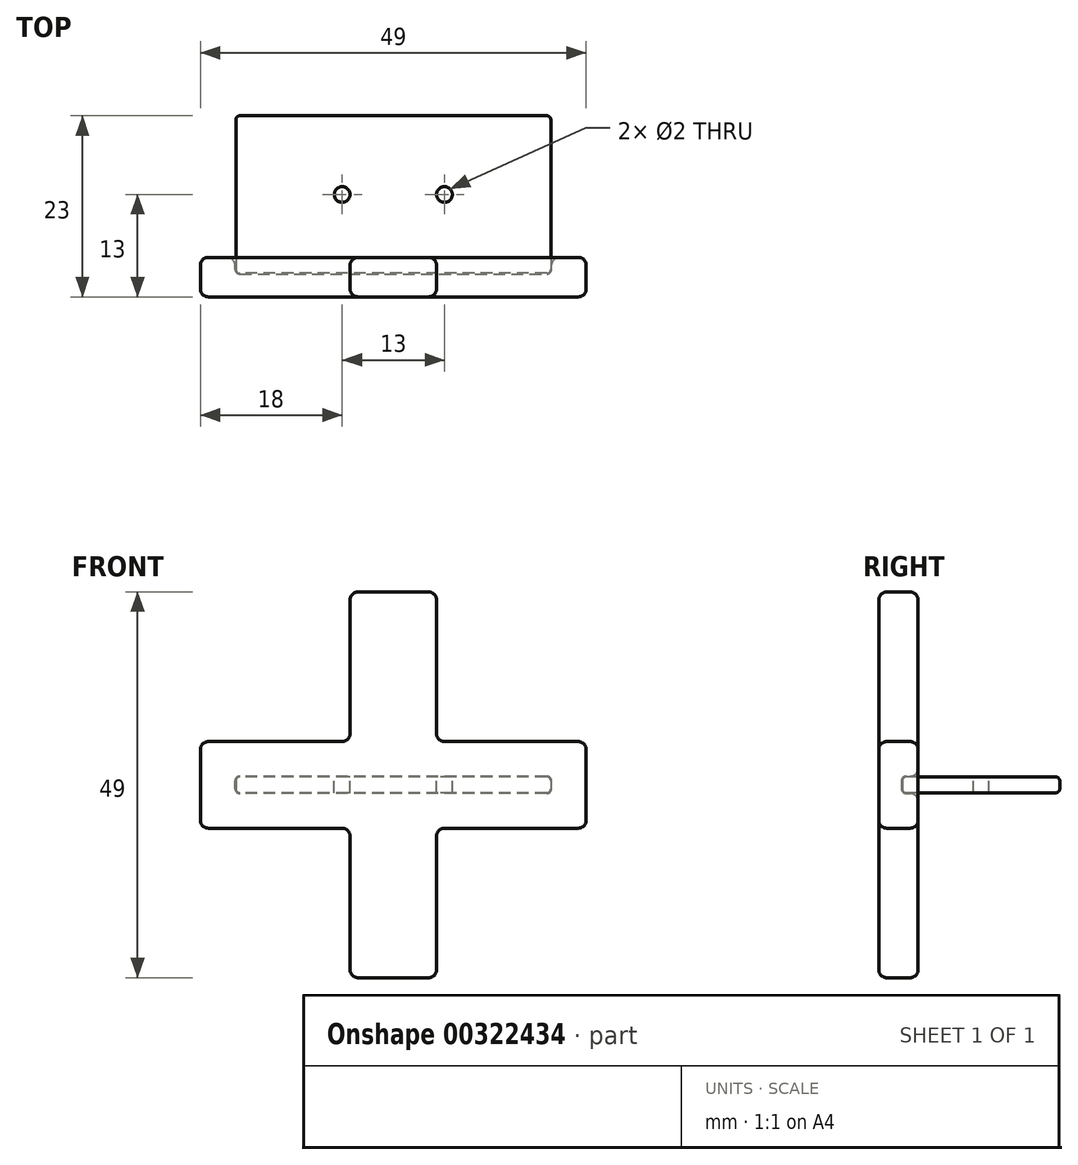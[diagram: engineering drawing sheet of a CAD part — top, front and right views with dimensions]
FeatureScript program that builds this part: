
annotation { "Feature Type Name" : "Feature", "Feature Type Description" : "" }
export const myFeature = defineFeature(function(context is Context, id is Id, definition is map)
    precondition{}
    {
        {
            var Q0;
            Q0=qCreatedBy(makeId("Top.planeOp"),FACE);
            var sketch = newSketch(context, id + "F0", { "sketchPlane" : qUnion([Q0])});
            skLineSegment(sketch, "E0.bottom", {"start": v(20, 10) * mm, "end": v(-20, 10) * mm});
            skLineSegment(sketch, "E0.top", {"start": v(20, -10) * mm, "end": v(-20, -10) * mm});
            skLineSegment(sketch, "E0.left", {"start": v(20, 10) * mm, "end": v(20, -10) * mm});
            skLineSegment(sketch, "E0.right", {"start": v(-20, 10) * mm, "end": v(-20, -10) * mm});
            skPoint(sketch, "E0.middle", {"position": v(0, 0) * mm});
            skSolve(sketch);
        }
        {
            var Q0;
            Q0=makeQuery(id+"F0.imprint","IMPRINT",FACE,{"disambiguationData":[TD([[makeQuery(id+"F0.imprint","IMPRINT",EDGE,{"derivedFrom":sQuery(id+"F0.wireOp",EDGE,"E0.bottom")}),1.0]])]});
            extrude(context, id + "F1", {"entities" : qUnion([Q0]), "depth" : 2 * mm});
        }
        {
            var Q0;
            Q0=makeQuery(id+"F1.opExtrude","SWEPT_FACE",FACE,{"disambiguationData":[OSD([sQuery(id+"F0.wireOp",EDGE,"E0.top")])]});
            var Q1;
            Q1=makeQuery(id+"F1.opExtrude","CAP_FACE",FACE,{"disambiguationData":[OSD([sQuery(id+"F0.wireOp",EDGE,"E0.bottom"),sQuery(id+"F0.wireOp",EDGE,"E0.top"),sQuery(id+"F0.wireOp",EDGE,"E0.left"),sQuery(id+"F0.wireOp",EDGE,"E0.right")])],"isStart":false});
            var Q2;
            Q2=makeQuery(id+"F1.opExtrude","CAP_FACE",FACE,{"disambiguationData":[OSD([sQuery(id+"F0.wireOp",EDGE,"E0.bottom"),sQuery(id+"F0.wireOp",EDGE,"E0.top"),sQuery(id+"F0.wireOp",EDGE,"E0.left"),sQuery(id+"F0.wireOp",EDGE,"E0.right")])],"isStart":true});
            var Q3;
            Q3=makeQuery(id+"F1.opExtrude","SWEPT_FACE",FACE,{"disambiguationData":[OSD([sQuery(id+"F0.wireOp",EDGE,"E0.right")])]});
            var Q4;
            Q4=makeQuery(id+"F1.opExtrude","SWEPT_FACE",FACE,{"disambiguationData":[OSD([sQuery(id+"F0.wireOp",EDGE,"E0.bottom")])]});
            var Q5;
            Q5=makeQuery(id+"F1.opExtrude","SWEPT_FACE",FACE,{"disambiguationData":[OSD([sQuery(id+"F0.wireOp",EDGE,"E0.left")])]});
            fillet(context, id + "F2", {"entities" : qUnion([Q0, Q1, Q2, Q3, Q4, Q5]), "radius" : 0.5 * mm, "tangentPropagation" : true, "allowEdgeOverflow" : false});
        }
        {
            var Q0;
            Q0=makeQuery(id+"F1.opExtrude","CAP_FACE",FACE,{"disambiguationData":[OSD([sQuery(id+"F0.wireOp",EDGE,"E0.bottom"),sQuery(id+"F0.wireOp",EDGE,"E0.top"),sQuery(id+"F0.wireOp",EDGE,"E0.left"),sQuery(id+"F0.wireOp",EDGE,"E0.right")])],"isStart":false});
            var sketch = newSketch(context, id + "F3", { "sketchPlane" : qUnion([Q0])});
            skCircle(sketch, "E1", {"center": v(-6.5, 0) * mm, "radius": 1 * mm});
            skCircle(sketch, "E2", {"center": v(6.5, 0) * mm, "radius": 1 * mm});
            skSolve(sketch);
        }
        {
            var Q0;
            Q0=makeQuery(id+"F3.imprint","IMPRINT",FACE,{"disambiguationData":[TD([[makeQuery(id+"F3.imprint","IMPRINT",EDGE,{"derivedFrom":sQuery(id+"F3.wireOp",EDGE,"E1")}),1.0]])]});
            var Q1;
            Q1=makeQuery(id+"F3.imprint","IMPRINT",FACE,{"disambiguationData":[TD([[makeQuery(id+"F3.imprint","IMPRINT",EDGE,{"derivedFrom":sQuery(id+"F3.wireOp",EDGE,"E2")}),1.0]])]});
            extrude(context, id + "F4", {"entities" : qUnion([Q0, Q1]), "operationType" : NewBodyOperationType.REMOVE, "oppositeDirection" : true, "depth" : 25 * mm});
        }
        {
            var Q0;
            Q0=makeQuery(id+"F1.opExtrude","SWEPT_FACE",FACE,{"disambiguationData":[OSD([sQuery(id+"F0.wireOp",EDGE,"E0.top")])]});
            var sketch = newSketch(context, id + "F5", { "sketchPlane" : qUnion([Q0])});
            skSolve(sketch);
        }
        {
            var Q0;
            {var subQ0=sQuery(id+"F0.wireOp",EDGE,"E0.top");var subQ1=makeQuery(id+"F1.opExtrude","SWEPT_FACE",FACE,{"disambiguationData":[OSD([subQ0])]});Q0=makeQuery(id+"F5.imprint","IMPRINT",FACE,{"disambiguationData":[TD([[makeQuery(id+"F5.imprint","IMPRINT",EDGE,{"derivedFrom":makeQuery(id+"F2.opFillet","BLEND_EDGE",EDGE,{"blendedFrom":[makeQuery(id+"F1.opExtrude","CAP_EDGE",EDGE,{"disambiguationData":[OSD([subQ0])],"isStart":true}),subQ1],"blendedInto":[subQ1]})}),1.0]])]});}
            var sketch = newSketch(context, id + "F6", { "sketchPlane" : qUnion([Q0])});
            skLineSegment(sketch, "E3.0", {"start": v(24.5, 6.5) * mm, "end": v(5.5, 6.5) * mm});
            skLineSegment(sketch, "E3.1", {"start": v(24.5, -4.5) * mm, "end": v(24.5, 6.5) * mm});
            skLineSegment(sketch, "E3.2", {"start": v(-24.5, -4.5) * mm, "end": v(24.5, -4.5) * mm});
            skLineSegment(sketch, "E3.3", {"start": v(-24.5, 6.5) * mm, "end": v(-24.5, -4.5) * mm});
            skLineSegment(sketch, "E4.bottom", {"start": v(5.5, -23.5) * mm, "end": v(-5.5, -23.5) * mm});
            skLineSegment(sketch, "E4.top", {"start": v(5.5, 25.5) * mm, "end": v(-5.5, 25.5) * mm});
            skLineSegment(sketch, "E4.left", {"start": v(5.5, -23.5) * mm, "end": v(5.5, -4.5) * mm});
            skLineSegment(sketch, "E4.right", {"start": v(-5.5, -23.5) * mm, "end": v(-5.5, -4.5) * mm});
            skPoint(sketch, "E4.middle", {"position": v(0, 6.5) * mm});
            skLineSegment(sketch, "E5.trimOffspring", {"start": v(-5.5, 6.5) * mm, "end": v(-24.5, 6.5) * mm});
            skLineSegment(sketch, "E6.trimOffspring", {"start": v(5.5, 6.5) * mm, "end": v(5.5, 25.5) * mm});
            skLineSegment(sketch, "E7.trimOffspring", {"start": v(-5.5, 6.5) * mm, "end": v(-5.5, 25.5) * mm});
            skPoint(sketch, "E8.0.3.end.orphan", {"position": v(19.5, 1.5) * mm});
            skPoint(sketch, "E8.0.3.start.orphan", {"position": v(19.5, 0.5) * mm});
            skPoint(sketch, "E8.0.1.end.orphan", {"position": v(-19.5, 0.5) * mm});
            skPoint(sketch, "E8.0.1.start.orphan", {"position": v(-19.5, 1.5) * mm});
            skSolve(sketch);
        }
        {
            var Q0;
            {var subQ0=sQuery(id+"F0.wireOp",EDGE,"E0.top");var subQ1=makeQuery(id+"F1.opExtrude","SWEPT_FACE",FACE,{"disambiguationData":[OSD([subQ0])]});Q0=makeQuery(id+"F6.imprint","IMPRINT",FACE,{"disambiguationData":[TD([[makeQuery(id+"F6.imprint","IMPRINT",EDGE,{"derivedFrom":makeQuery(id+"F5.imprint","IMPRINT",EDGE,{"derivedFrom":makeQuery(id+"F2.opFillet","BLEND_EDGE",EDGE,{"blendedFrom":[makeQuery(id+"F1.opExtrude","CAP_EDGE",EDGE,{"disambiguationData":[OSD([subQ0])],"isStart":true}),subQ1],"blendedInto":[subQ1]})})}),1.0]])]});}
            var Q1;
            Q1=makeQuery(id+"F6.imprint","IMPRINT",FACE,{"disambiguationData":[TD([[makeQuery(id+"F6.imprint","IMPRINT",EDGE,{"derivedFrom":sQuery(id+"F6.wireOp",EDGE,"E3.0")}),1.0]])]});
            var Q2;
            Q2=makeQuery(id+"F6.imprint","IMPRINT",FACE,{"disambiguationData":[TD([[makeQuery(id+"F6.imprint","IMPRINT",EDGE,{"derivedFrom":sQuery(id+"F6.wireOp",EDGE,"E4.bottom")}),-1.0]])]});
            extrude(context, id + "F7", {"entities" : qUnion([Q0, Q1, Q2]), "depth" : 3 * mm, "hasSecondDirection" : true, "secondDirectionOppositeDirection" : true, "secondDirectionDepth" : 2 * mm});
        }
        {
            var Q0;
            Q0=makeQuery(id+"F1.opExtrude","SWEPT_BODY",BODY,{"disambiguationData":[OSD([sQuery(id+"F0.wireOp",EDGE,"E0.bottom"),sQuery(id+"F0.wireOp",EDGE,"E0.top"),sQuery(id+"F0.wireOp",EDGE,"E0.left"),sQuery(id+"F0.wireOp",EDGE,"E0.right")])]});
            var Q1;
            Q1=makeQuery(id+"F7.opExtrude","SWEPT_BODY",BODY,{"disambiguationData":[OSD([sQuery(id+"F6.wireOp",EDGE,"E3.0"),sQuery(id+"F6.wireOp",EDGE,"E3.1"),sQuery(id+"F6.wireOp",EDGE,"E3.2"),sQuery(id+"F6.wireOp",EDGE,"E3.3"),sQuery(id+"F6.wireOp",EDGE,"E4.bottom"),sQuery(id+"F6.wireOp",EDGE,"E4.top"),sQuery(id+"F6.wireOp",EDGE,"E4.left"),sQuery(id+"F6.wireOp",EDGE,"E4.right"),sQuery(id+"F6.wireOp",EDGE,"E5.trimOffspring"),sQuery(id+"F6.wireOp",EDGE,"E6.trimOffspring"),sQuery(id+"F6.wireOp",EDGE,"E7.trimOffspring")])]});
            booleanBodies(context, id + "F8", {"operationType" : BooleanOperationType.SUBTRACTION, "tools" : qUnion([Q0]), "targets" : qUnion([Q1]), "offset" : true, "offsetAll" : true, "offsetDistance" : 0.1 * mm, "keepTools" : true});
        }
        {
            var Q0;
            Q0=makeQuery(id+"F7.opExtrude","CAP_FACE",FACE,{"disambiguationData":[OSD([sQuery(id+"F6.wireOp",EDGE,"E3.0"),sQuery(id+"F6.wireOp",EDGE,"E3.1"),sQuery(id+"F6.wireOp",EDGE,"E3.2"),sQuery(id+"F6.wireOp",EDGE,"E3.3"),sQuery(id+"F6.wireOp",EDGE,"E4.bottom"),sQuery(id+"F6.wireOp",EDGE,"E4.top"),sQuery(id+"F6.wireOp",EDGE,"E4.left"),sQuery(id+"F6.wireOp",EDGE,"E4.right"),sQuery(id+"F6.wireOp",EDGE,"E5.trimOffspring"),sQuery(id+"F6.wireOp",EDGE,"E6.trimOffspring"),sQuery(id+"F6.wireOp",EDGE,"E7.trimOffspring")])],"isStart":true});
            var Q1;
            Q1=makeQuery(id+"F7.opExtrude","CAP_FACE",FACE,{"disambiguationData":[OSD([sQuery(id+"F6.wireOp",EDGE,"E3.0"),sQuery(id+"F6.wireOp",EDGE,"E3.1"),sQuery(id+"F6.wireOp",EDGE,"E3.2"),sQuery(id+"F6.wireOp",EDGE,"E3.3"),sQuery(id+"F6.wireOp",EDGE,"E4.bottom"),sQuery(id+"F6.wireOp",EDGE,"E4.top"),sQuery(id+"F6.wireOp",EDGE,"E4.left"),sQuery(id+"F6.wireOp",EDGE,"E4.right"),sQuery(id+"F6.wireOp",EDGE,"E5.trimOffspring"),sQuery(id+"F6.wireOp",EDGE,"E6.trimOffspring"),sQuery(id+"F6.wireOp",EDGE,"E7.trimOffspring")])],"isStart":false});
            var Q2;
            {var subQ0=sQuery(id+"F6.wireOp",EDGE,"E3.2");Q2=makeQuery(id+"F7.opExtrude","SWEPT_FACE",FACE,{"disambiguationData":[OSD([subQ0]),TDD([makeQuery(id+"F6.imprint","IMPRINT",EDGE,{"disambiguationData":[TD([[makeQuery(id+"F6.imprint","INTERSECT",VERTEX,{"derivedFrom":[sQuery(id+"F6.wireOp",EDGE,"E3.1"),subQ0]}),1.0]])],"derivedFrom":subQ0})])]});}
            var Q3;
            Q3=makeQuery(id+"F7.opExtrude","SWEPT_FACE",FACE,{"disambiguationData":[OSD([sQuery(id+"F6.wireOp",EDGE,"E4.left")])]});
            var Q4;
            Q4=makeQuery(id+"F7.opExtrude","SWEPT_FACE",FACE,{"disambiguationData":[OSD([sQuery(id+"F6.wireOp",EDGE,"E4.bottom")])]});
            var Q5;
            Q5=makeQuery(id+"F7.opExtrude","SWEPT_FACE",FACE,{"disambiguationData":[OSD([sQuery(id+"F6.wireOp",EDGE,"E3.1")])]});
            var Q6;
            Q6=makeQuery(id+"F7.opExtrude","SWEPT_FACE",FACE,{"disambiguationData":[OSD([sQuery(id+"F6.wireOp",EDGE,"E3.0")])]});
            var Q7;
            Q7=makeQuery(id+"F7.opExtrude","SWEPT_FACE",FACE,{"disambiguationData":[OSD([sQuery(id+"F6.wireOp",EDGE,"E6.trimOffspring")])]});
            var Q8;
            Q8=makeQuery(id+"F7.opExtrude","SWEPT_FACE",FACE,{"disambiguationData":[OSD([sQuery(id+"F6.wireOp",EDGE,"E4.top")])]});
            var Q9;
            Q9=makeQuery(id+"F7.opExtrude","SWEPT_FACE",FACE,{"disambiguationData":[OSD([sQuery(id+"F6.wireOp",EDGE,"E7.trimOffspring")])]});
            var Q10;
            Q10=makeQuery(id+"F7.opExtrude","SWEPT_FACE",FACE,{"disambiguationData":[OSD([sQuery(id+"F6.wireOp",EDGE,"E5.trimOffspring")])]});
            var Q11;
            Q11=makeQuery(id+"F7.opExtrude","SWEPT_FACE",FACE,{"disambiguationData":[OSD([sQuery(id+"F6.wireOp",EDGE,"E3.3")])]});
            var Q12;
            {var subQ0=sQuery(id+"F6.wireOp",EDGE,"E3.2");Q12=makeQuery(id+"F7.opExtrude","SWEPT_FACE",FACE,{"disambiguationData":[OSD([subQ0]),TDD([makeQuery(id+"F6.imprint","IMPRINT",EDGE,{"disambiguationData":[TD([[makeQuery(id+"F6.imprint","INTERSECT",VERTEX,{"derivedFrom":[subQ0,sQuery(id+"F6.wireOp",EDGE,"E3.3")]}),-1.0]])],"derivedFrom":subQ0})])]});}
            fillet(context, id + "F9", {"entities" : qUnion([Q0, Q1, Q2, Q3, Q4, Q5, Q6, Q7, Q8, Q9, Q10, Q11, Q12]), "radius" : 1 * mm, "tangentPropagation" : true, "allowEdgeOverflow" : false});
        }
    });
